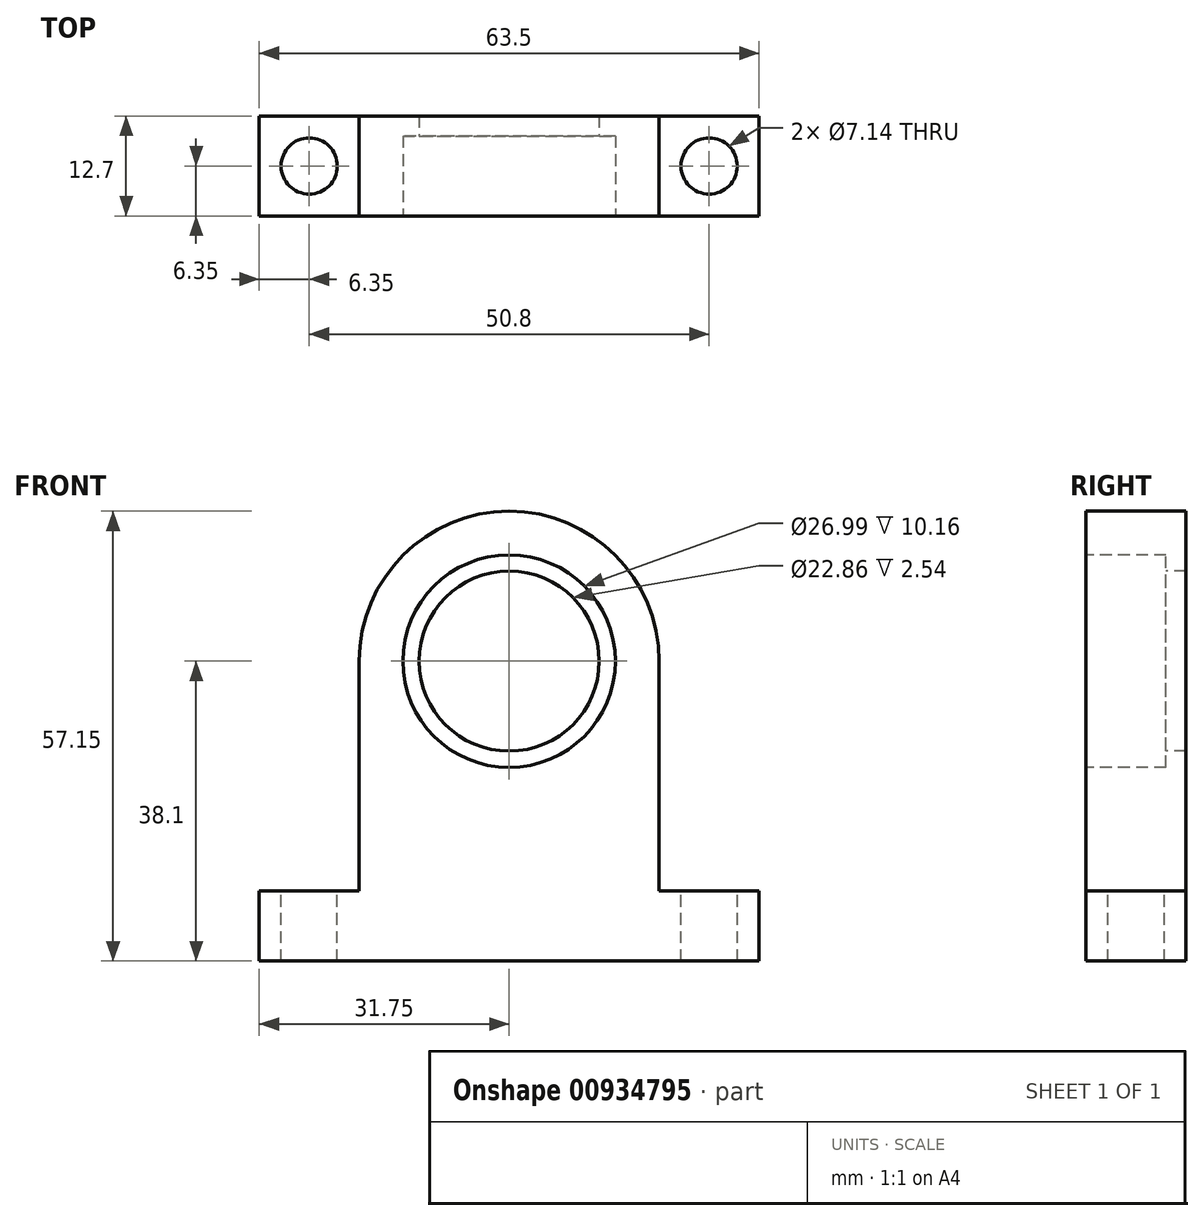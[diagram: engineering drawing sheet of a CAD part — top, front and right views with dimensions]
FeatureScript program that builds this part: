
annotation { "Feature Type Name" : "Feature", "Feature Type Description" : "" }
export const myFeature = defineFeature(function(context is Context, id is Id, definition is map)
    precondition{}
    {
        {
            var Q0;
            Q0=qCreatedBy(makeId("Front.planeOp"),FACE);
            var sketch = newSketch(context, id + "F0", { "sketchPlane" : qUnion([Q0])});
            skLineSegment(sketch, "E0.bottom", {"start": v(31.75, -19.05) * mm, "end": v(-31.75, -19.05) * mm});
            skLineSegment(sketch, "E0.top", {"start": v(31.75, 19.05) * mm, "end": v(-31.75, 19.05) * mm});
            skLineSegment(sketch, "E0.left", {"start": v(31.75, -19.05) * mm, "end": v(31.75, 19.05) * mm});
            skLineSegment(sketch, "E0.right", {"start": v(-31.75, -19.05) * mm, "end": v(-31.75, 19.05) * mm});
            skPoint(sketch, "E0.middle", {"position": v(0, 0) * mm});
            skSolve(sketch);
        }
        {
            var Q0;
            Q0=makeQuery(id+"F0.imprint","IMPRINT",FACE,{"disambiguationData":[TD([[makeQuery(id+"F0.imprint","IMPRINT",EDGE,{"derivedFrom":sQuery(id+"F0.wireOp",EDGE,"E0.bottom")}),-1.0]])]});
            extrude(context, id + "F1", {"entities" : qUnion([Q0]), "endBound" : BoundingType.SYMMETRIC, "depth" : 12.7 * mm, "offsetDistance" : 25.4 * mm});
        }
        {
            var Q0;
            Q0=makeQuery(id+"F1.opExtrude","CAP_FACE",FACE,{"disambiguationData":[OSD([sQuery(id+"F0.wireOp",EDGE,"E0.bottom"),sQuery(id+"F0.wireOp",EDGE,"E0.top"),sQuery(id+"F0.wireOp",EDGE,"E0.left"),sQuery(id+"F0.wireOp",EDGE,"E0.right")])],"isStart":false});
            var sketch = newSketch(context, id + "F2", { "sketchPlane" : qUnion([Q0])});
            skLineSegment(sketch, "E1.bottom", {"start": v(-31.75, 19.05) * mm, "end": v(-19.05, 19.05) * mm});
            skLineSegment(sketch, "E1.top", {"start": v(-31.75, -10.16) * mm, "end": v(-19.05, -10.16) * mm});
            skLineSegment(sketch, "E1.left", {"start": v(-31.75, 19.05) * mm, "end": v(-31.75, -10.16) * mm});
            skLineSegment(sketch, "E1.right", {"start": v(-19.05, 19.05) * mm, "end": v(-19.05, -10.16) * mm});
            skLineSegment(sketch, "E2.bottom", {"start": v(31.75, 19.05) * mm, "end": v(19.05, 19.05) * mm});
            skLineSegment(sketch, "E2.top", {"start": v(31.75, -10.16) * mm, "end": v(19.05, -10.16) * mm});
            skLineSegment(sketch, "E2.left", {"start": v(31.75, 19.05) * mm, "end": v(31.75, -10.16) * mm});
            skLineSegment(sketch, "E2.right", {"start": v(19.05, 19.05) * mm, "end": v(19.05, -10.16) * mm});
            skSolve(sketch);
        }
        {
            var Q0;
            Q0=makeQuery(id+"F2.imprint","IMPRINT",FACE,{"disambiguationData":[TD([[makeQuery(id+"F2.imprint","IMPRINT",EDGE,{"derivedFrom":sQuery(id+"F2.wireOp",EDGE,"E1.bottom")}),1.0]])]});
            var Q1;
            Q1=makeQuery(id+"F2.imprint","IMPRINT",FACE,{"disambiguationData":[TD([[makeQuery(id+"F2.imprint","IMPRINT",EDGE,{"derivedFrom":sQuery(id+"F2.wireOp",EDGE,"E2.bottom")}),1.0]])]});
            extrude(context, id + "F3", {"entities" : qUnion([Q0, Q1]), "operationType" : NewBodyOperationType.REMOVE, "endBound" : BoundingType.THROUGH_ALL, "oppositeDirection" : true, "depth" : 25.4 * mm, "offsetDistance" : 25.4 * mm});
        }
        {
            var Q0;
            Q0=qCreatedBy(makeId("Front.planeOp"),FACE);
            var sketch = newSketch(context, id + "F4", { "sketchPlane" : qUnion([Q0])});
            skArc(sketch, "E3", {"start": v(19.05, 19.05) * mm, "mid": v(0, 38.1) * mm, "end": v(-19.05, 19.05) * mm});
            skLineSegment(sketch, "E4", {"start": v(-19.05, 19.05) * mm, "end": v(19.05, 19.05) * mm});
            skSolve(sketch);
        }
        {
            var Q0;
            Q0=makeQuery(id+"F4.imprint","IMPRINT",FACE,{"disambiguationData":[TD([[makeQuery(id+"F4.imprint","IMPRINT",EDGE,{"derivedFrom":sQuery(id+"F4.wireOp",EDGE,"E3")}),1.0]])]});
            var Q1;
            Q1=makeQuery(id+"F1.opExtrude","CAP_FACE",FACE,{"disambiguationData":[OSD([sQuery(id+"F0.wireOp",EDGE,"E0.bottom"),sQuery(id+"F0.wireOp",EDGE,"E0.top"),sQuery(id+"F0.wireOp",EDGE,"E0.left"),sQuery(id+"F0.wireOp",EDGE,"E0.right")])],"isStart":false});
            var Q2;
            Q2=makeQuery(id+"F1.opExtrude","CAP_FACE",FACE,{"disambiguationData":[OSD([sQuery(id+"F0.wireOp",EDGE,"E0.bottom"),sQuery(id+"F0.wireOp",EDGE,"E0.top"),sQuery(id+"F0.wireOp",EDGE,"E0.left"),sQuery(id+"F0.wireOp",EDGE,"E0.right")])],"isStart":true});
            extrude(context, id + "F5", {"entities" : qUnion([Q0]), "operationType" : NewBodyOperationType.ADD, "endBound" : BoundingType.UP_TO_SURFACE, "depth" : 25.4 * mm, "endBoundEntityFace" : qUnion([Q1]), "offsetDistance" : 25.4 * mm, "hasSecondDirection" : true, "secondDirectionBound" : SecondDirectionBoundingType.UP_TO_SURFACE, "secondDirectionOppositeDirection" : true, "secondDirectionDepth" : 25.4 * mm, "secondDirectionBoundEntityFace" : qUnion([Q2])});
        }
        {
            var Q0;
            Q0=makeQuery(id+"F5.boolean.opBoolean","MERGE",FACE,{"derivedFrom":[makeQuery(id+"F1.opExtrude","CAP_FACE",FACE,{"disambiguationData":[OSD([sQuery(id+"F0.wireOp",EDGE,"E0.bottom"),sQuery(id+"F0.wireOp",EDGE,"E0.top"),sQuery(id+"F0.wireOp",EDGE,"E0.left"),sQuery(id+"F0.wireOp",EDGE,"E0.right")])],"isStart":false}),makeQuery(id+"F5.opExtrude","CAP_FACE",FACE,{"disambiguationData":[OSD([sQuery(id+"F4.wireOp",EDGE,"E3"),sQuery(id+"F4.wireOp",EDGE,"E4")])],"isStart":false})]});
            var sketch = newSketch(context, id + "F6", { "sketchPlane" : qUnion([Q0])});
            skCircle(sketch, "E5", {"center": v(0, 19.05) * mm, "radius": 13.5 * mm});
            skSolve(sketch);
        }
        {
            var Q0;
            Q0=makeQuery(id+"F6.imprint","IMPRINT",FACE,{"disambiguationData":[TD([[makeQuery(id+"F6.imprint","IMPRINT",EDGE,{"derivedFrom":sQuery(id+"F6.wireOp",EDGE,"E5")}),1.0]])]});
            var Q1;
            Q1=sQuery(id+"F6.wireOp",EDGE,"E5");
            extrude(context, id + "F7", {"entities" : qUnion([Q0]), "operationType" : NewBodyOperationType.REMOVE, "surfaceEntities" : qUnion([Q1]), "oppositeDirection" : true, "depth" : 10.16 * mm, "offsetDistance" : 25.4 * mm});
        }
        {
            var Q0;
            Q0=makeQuery(id+"F7.boolean.opBoolean","COPY",FACE,{"derivedFrom":makeQuery(id+"F7.opExtrude","CAP_FACE",FACE,{"disambiguationData":[OSD([sQuery(id+"F6.wireOp",EDGE,"E5")])],"isStart":false})});
            var sketch = newSketch(context, id + "F8", { "sketchPlane" : qUnion([Q0])});
            skCircle(sketch, "E6", {"center": v(0, 19.05) * mm, "radius": 11.43 * mm});
            skSolve(sketch);
        }
        {
            var Q0;
            Q0=makeQuery(id+"F8.imprint","IMPRINT",FACE,{"disambiguationData":[TD([[makeQuery(id+"F8.imprint","IMPRINT",EDGE,{"derivedFrom":sQuery(id+"F8.wireOp",EDGE,"E6")}),1.0]])]});
            extrude(context, id + "F9", {"entities" : qUnion([Q0]), "operationType" : NewBodyOperationType.REMOVE, "oppositeDirection" : true, "depth" : 25.4 * mm, "offsetDistance" : 25.4 * mm});
        }
        {
            var Q0;
            Q0=makeQuery(id+"F3.boolean.opBoolean","COPY",FACE,{"derivedFrom":makeQuery(id+"F3.opExtrude","SWEPT_FACE",FACE,{"disambiguationData":[OSD([sQuery(id+"F2.wireOp",EDGE,"E1.top")])]})});
            var sketch = newSketch(context, id + "F10", { "sketchPlane" : qUnion([Q0])});
            skPoint(sketch, "E7", {"position": v(-25.4, 0) * mm});
            skPoint(sketch, "E8", {"position": v(25.4, 0) * mm});
            skSolve(sketch);
        }
        {
            var Q0;
            Q0=sQuery(id+"F10.wireOp",VERTEX,"E7");
            var Q1;
            Q1=sQuery(id+"F10.wireOp",VERTEX,"E8");
            var Q2;
            Q2=makeQuery(id+"F1.opExtrude","SWEPT_BODY",BODY,{"disambiguationData":[OSD([sQuery(id+"F0.wireOp",EDGE,"E0.bottom"),sQuery(id+"F0.wireOp",EDGE,"E0.top"),sQuery(id+"F0.wireOp",EDGE,"E0.left"),sQuery(id+"F0.wireOp",EDGE,"E0.right")])]});
            hole(context, id + "F11", {"style" : HoleStyle.SIMPLE, "endStyle" : HoleEndStyle.THROUGH, "standardTappedOrClearance" : lookupTablePath({ "fit" : "Normal (ASME)", "standard" : "ANSI", "size" : "1/4", "type" : "Clearance" }), "standardBlindInLast" : lookupTablePath({ "fit" : "Normal", "standard" : "ANSI", "engagement" : "75%", "pitch" : "20 tpi", "size" : "1/4", "type" : "Clearance & tapped" }), "holeDiameter" : 7.14 * mm, "majorDiameter" : 6.35 * mm, "isTappedThrough" : true, "tappedDepth" : 12.7 * mm, "tapClearance" : 3, "startFromSketch" : true, "locations" : qUnion([Q0, Q1]), "scope" : qUnion([Q2])});
        }
    });
